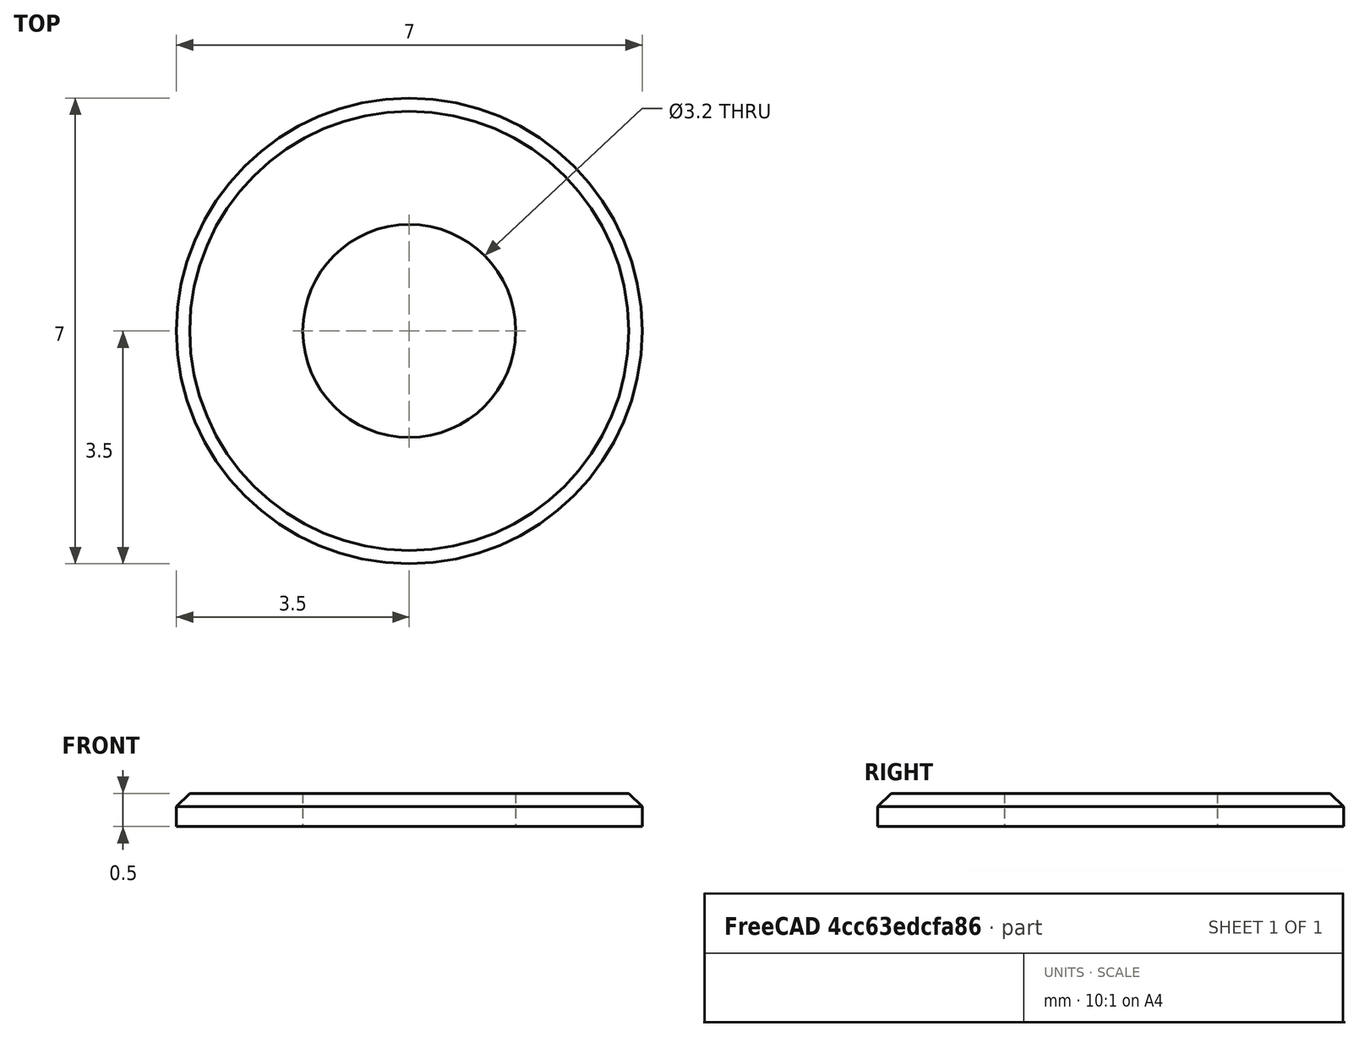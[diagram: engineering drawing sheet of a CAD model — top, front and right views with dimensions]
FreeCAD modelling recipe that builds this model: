
FCSTD DOCUMENT  (FreeCAD 0.15R4651 (Git))
Label: Scheibe_DIN125-B 3,2
License: CC-BY 3.0
LicenseURL: http://creativecommons.org/licenses/by/3.0/
objects: Sketcher::SketchObject×1, PartDesign::Revolution×1
note: 3 computed .brp shape members not serialized (recipe doc carries the construction recipe); baked Part::Feature solids carry a one-line shape summary decoded from their .brp

FEATURE [Sketcher::SketchObject] Sketch
  Placement = pos=(0,0,0) rot=(0.57735,0.57735,0.57735;2.0944rad)
  sketch-geometry (5):
    g0: LineSegment StartX=1.6 StartY=0 StartZ=0 EndX=3.5 EndY=0 EndZ=0
    g1: LineSegment StartX=3.5 StartY=0 StartZ=0 EndX=3.5 EndY=0.3 EndZ=0
    g2: LineSegment StartX=3.3 StartY=0.5 StartZ=0 EndX=1.6 EndY=0.5 EndZ=0
    g3: LineSegment StartX=1.6 StartY=0.5 StartZ=0 EndX=1.6 EndY=0 EndZ=0
    g4: LineSegment StartX=3.3 StartY=0.5 StartZ=0 EndX=3.5 EndY=0.3 EndZ=0
  constraints (15):
    c: Coincident(g0,g1)
    c: Coincident(g2,g3)
    c: Coincident(g3,g0)
    c: Horizontal(g0)
    c: Horizontal(g2)
    c: Vertical(g1)
    c: Vertical(g3)
    c: PointOnObject(g0,g-1)
    c: DistanceX(g-1,g2) = 1.6
    c: Coincident(g2,g4)
    c: Coincident(g1,g4)
    c: DistanceX(g-1,g1) = 3.5
    c: DistanceY(g3) = -0.5
    c: DistanceX(g4) = 0.2
    c: DistanceY(g4) = -0.2
FEATURE [PartDesign::Revolution] Revolution  label="Scheibe DIN 125 - B 3,2 #"
  Angle = 360
  Axis = (0,0,1)
  Base = (0,0,0)
  Placement = pos=(0,0,0) rot=(0.57735,0.57735,0.57735;2.0944rad)
  ReferenceAxis = -> Sketch [V_Axis]
  Reversed = true
  Sketch = -> Sketch
